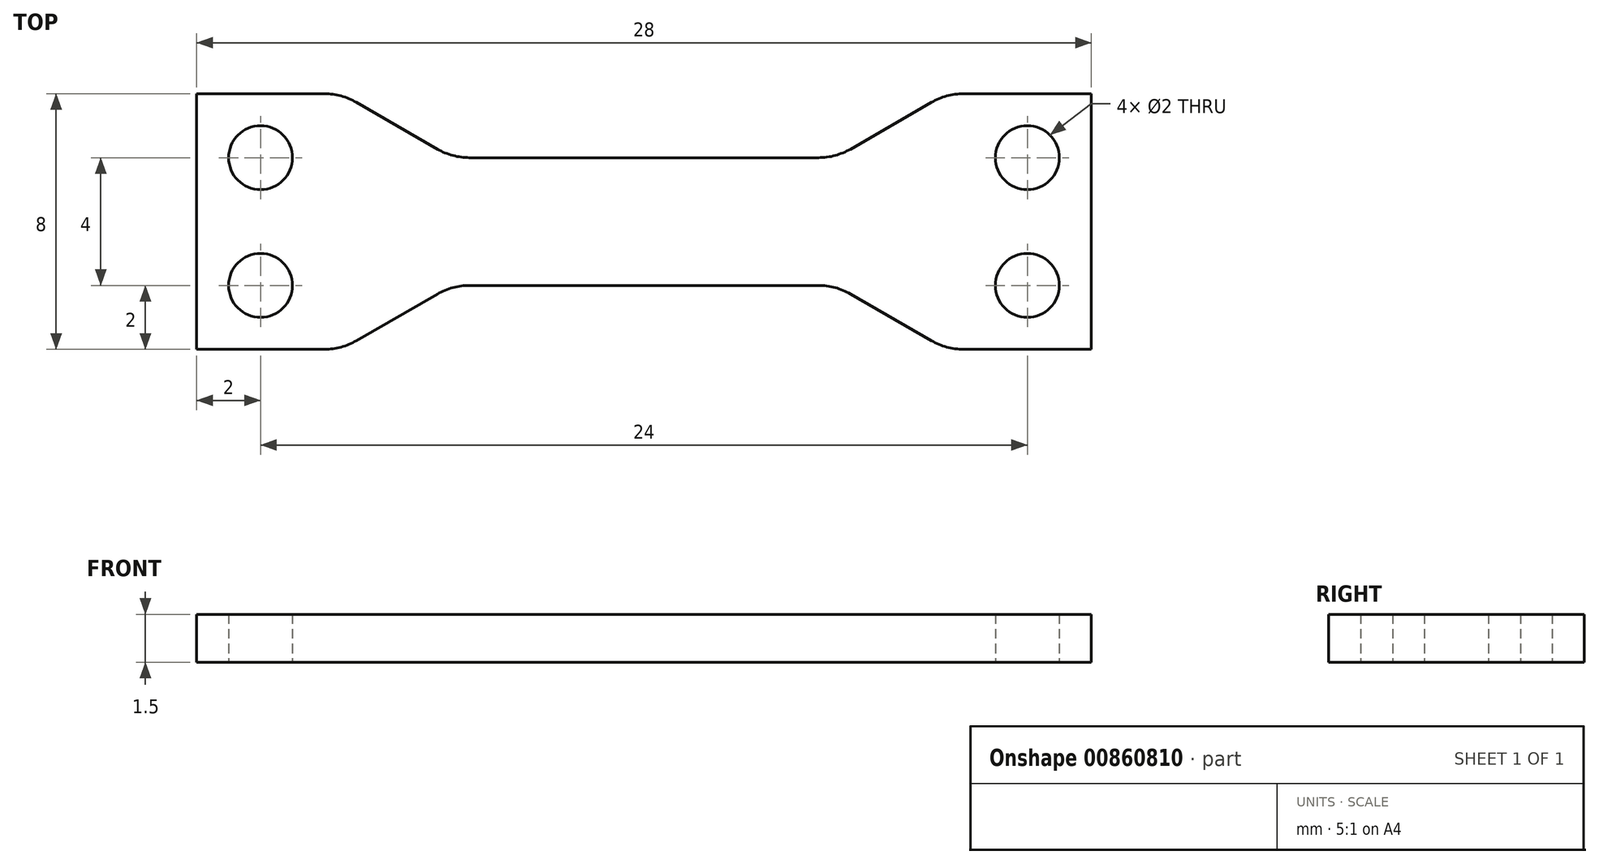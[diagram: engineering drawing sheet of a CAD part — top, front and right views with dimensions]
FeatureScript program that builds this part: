
annotation { "Feature Type Name" : "Feature", "Feature Type Description" : "" }
export const myFeature = defineFeature(function(context is Context, id is Id, definition is map)
    precondition{}
    {
        {
            var Q0;
            Q0=qCreatedBy(makeId("Top.planeOp"),FACE);
            var sketch = newSketch(context, id + "F0", { "sketchPlane" : qUnion([Q0])});
            skLineSegment(sketch, "E0", {"start": v(9, -3.73) * mm, "end": v(6.46, -2.27) * mm});
            skArc(sketch, "E1", {"start": v(6.46, -2.27) * mm, "mid": v(5.98, -2.07) * mm, "end": v(5.46, -2) * mm});
            skLineSegment(sketch, "E2", {"start": v(5.46, -2) * mm, "end": v(-5.46, -2) * mm});
            skArc(sketch, "E3", {"start": v(-5.46, -2) * mm, "mid": v(-5.98, -2.07) * mm, "end": v(-6.46, -2.27) * mm});
            skLineSegment(sketch, "E4", {"start": v(-6.46, -2.27) * mm, "end": v(-9, -3.73) * mm});
            skArc(sketch, "E5", {"start": v(-9, -3.73) * mm, "mid": v(-9.48, -3.93) * mm, "end": v(-10, -4) * mm});
            skLineSegment(sketch, "E6", {"start": v(-10, -4) * mm, "end": v(-14, -4) * mm});
            skLineSegment(sketch, "E7", {"start": v(-14, -4) * mm, "end": v(-14, 4) * mm});
            skLineSegment(sketch, "E8", {"start": v(-14, 4) * mm, "end": v(-10, 4) * mm});
            skArc(sketch, "E9", {"start": v(-10, 4) * mm, "mid": v(-9.48, 3.93) * mm, "end": v(-9, 3.73) * mm});
            skLineSegment(sketch, "E10", {"start": v(-9, 3.73) * mm, "end": v(-6.46, 2.27) * mm});
            skArc(sketch, "E11", {"start": v(-6.46, 2.27) * mm, "mid": v(-5.98, 2.07) * mm, "end": v(-5.46, 2) * mm});
            skLineSegment(sketch, "E12", {"start": v(-5.46, 2) * mm, "end": v(5.46, 2) * mm});
            skArc(sketch, "E13", {"start": v(5.46, 2) * mm, "mid": v(5.98, 2.07) * mm, "end": v(6.46, 2.27) * mm});
            skLineSegment(sketch, "E14", {"start": v(6.46, 2.27) * mm, "end": v(9, 3.73) * mm});
            skArc(sketch, "E15", {"start": v(9, 3.73) * mm, "mid": v(9.48, 3.93) * mm, "end": v(10, 4) * mm});
            skLineSegment(sketch, "E16", {"start": v(10, 4) * mm, "end": v(14, 4) * mm});
            skLineSegment(sketch, "E17", {"start": v(14, 4) * mm, "end": v(14, -4) * mm});
            skLineSegment(sketch, "E18", {"start": v(14, -4) * mm, "end": v(10, -4) * mm});
            skArc(sketch, "E19", {"start": v(10, -4) * mm, "mid": v(9.48, -3.93) * mm, "end": v(9, -3.73) * mm});
            skCircle(sketch, "E20", {"center": v(-12, 2) * mm, "radius": 1 * mm});
            skCircle(sketch, "E21", {"center": v(-12, -2) * mm, "radius": 1 * mm});
            skCircle(sketch, "E22", {"center": v(12, 2) * mm, "radius": 1 * mm});
            skCircle(sketch, "E23", {"center": v(12, -2) * mm, "radius": 1 * mm});
            skSolve(sketch);
        }
        {
            var Q0;
            Q0 = qSketchRegion(id + "F0", true);
            extrude(context, id + "F1", {"entities" : qUnion([Q0]), "depth" : 1.5 * mm, "offsetDistance" : 25 * mm});
        }
    });
